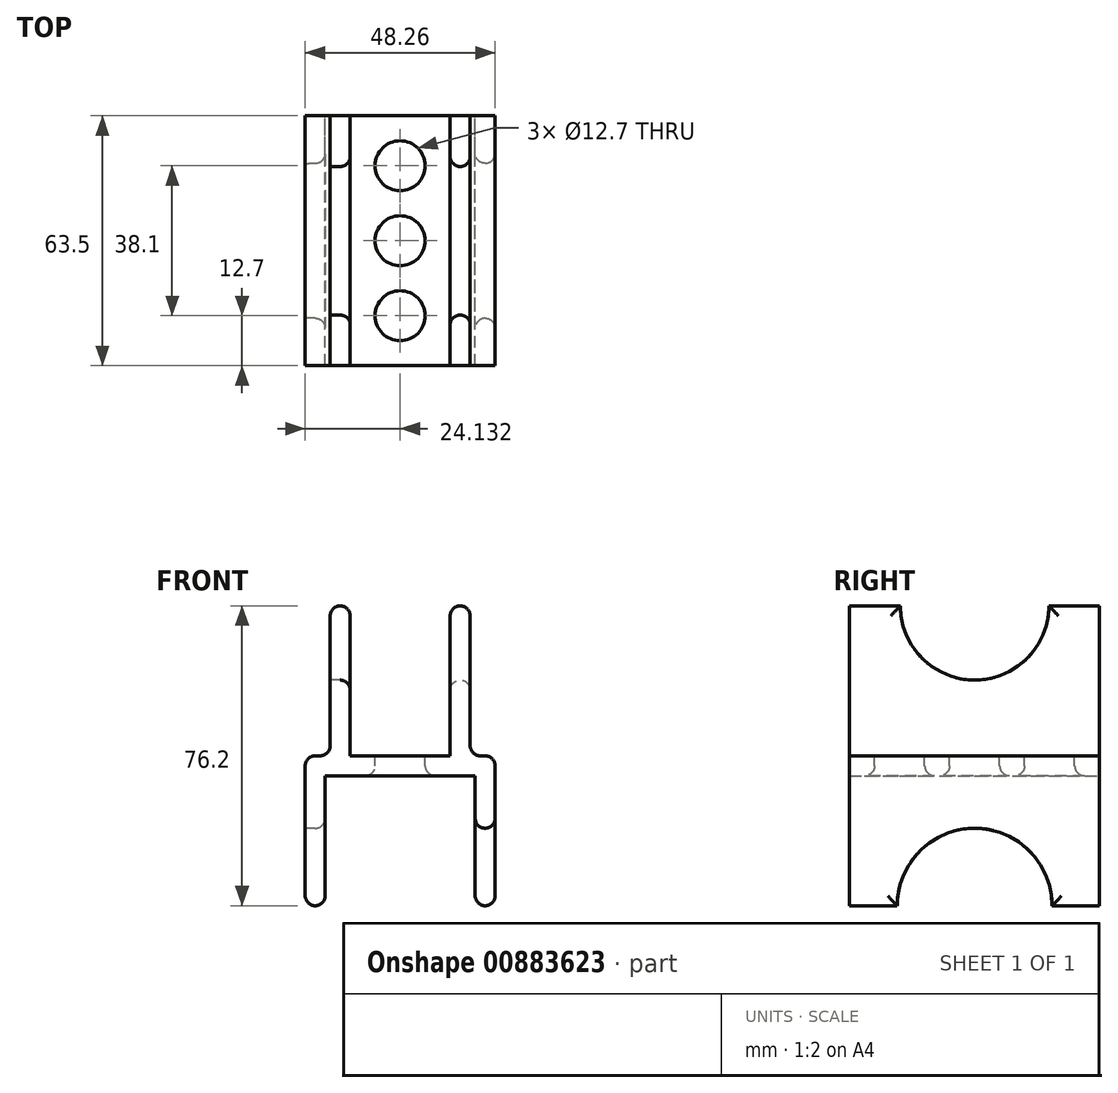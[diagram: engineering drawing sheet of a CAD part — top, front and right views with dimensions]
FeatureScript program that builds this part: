
annotation { "Feature Type Name" : "Feature", "Feature Type Description" : "" }
export const myFeature = defineFeature(function(context is Context, id is Id, definition is map)
    precondition{}
    {
        {
            var Q0;
            Q0=qCreatedBy(makeId("Front.planeOp"),FACE);
            var sketch = newSketch(context, id + "F0", { "sketchPlane" : qUnion([Q0])});
            skLineSegment(sketch, "E0", {"start": v(-15.34, 51.9) * mm, "end": v(-10.26, 51.9) * mm});
            skLineSegment(sketch, "E1", {"start": v(-10.26, 51.9) * mm, "end": v(-10.26, 13.8) * mm});
            skLineSegment(sketch, "E2", {"start": v(-10.26, 13.8) * mm, "end": v(15.14, 13.8) * mm});
            skLineSegment(sketch, "E3", {"start": v(15.14, 13.8) * mm, "end": v(15.14, 51.9) * mm});
            skLineSegment(sketch, "E4", {"start": v(15.14, 51.9) * mm, "end": v(20.22, 51.9) * mm});
            skLineSegment(sketch, "E5", {"start": v(20.22, 51.9) * mm, "end": v(20.22, 13.8) * mm});
            skLineSegment(sketch, "E6", {"start": v(20.22, 13.8) * mm, "end": v(26.57, 13.8) * mm});
            skLineSegment(sketch, "E7", {"start": v(26.57, 13.8) * mm, "end": v(26.57, -24.3) * mm});
            skLineSegment(sketch, "E8", {"start": v(26.57, -24.3) * mm, "end": v(21.5, -24.3) * mm});
            skLineSegment(sketch, "E9", {"start": v(21.5, -24.3) * mm, "end": v(21.5, 8.72) * mm});
            skLineSegment(sketch, "E10", {"start": v(21.5, 8.72) * mm, "end": v(-16.6, 8.72) * mm});
            skLineSegment(sketch, "E11", {"start": v(-16.6, 8.72) * mm, "end": v(-16.6, -24.3) * mm});
            skLineSegment(sketch, "E12", {"start": v(-16.6, -24.3) * mm, "end": v(-21.69, -24.3) * mm});
            skLineSegment(sketch, "E13", {"start": v(-21.69, -24.3) * mm, "end": v(-21.69, 13.8) * mm});
            skLineSegment(sketch, "E14", {"start": v(-21.69, 13.8) * mm, "end": v(-15.34, 13.8) * mm});
            skLineSegment(sketch, "E15", {"start": v(-15.34, 13.8) * mm, "end": v(-15.34, 51.9) * mm});
            skSolve(sketch);
        }
        {
            var Q0;
            Q0=makeQuery(id+"F0.imprint","IMPRINT",FACE,{"disambiguationData":[TD([[makeQuery(id+"F0.imprint","IMPRINT",EDGE,{"derivedFrom":sQuery(id+"F0.wireOp",EDGE,"E0")}),-1.0]])]});
            extrude(context, id + "F1", {"entities" : qUnion([Q0]), "depth" : 63.5 * mm, "offsetDistance" : 25.4 * mm});
        }
        {
            var Q0;
            Q0=makeQuery(id+"F1.opExtrude","SWEPT_FACE",FACE,{"disambiguationData":[OSD([sQuery(id+"F0.wireOp",EDGE,"E13")])]});
            var sketch = newSketch(context, id + "F2", { "sketchPlane" : qUnion([Q0])});
            skCircle(sketch, "E16", {"center": v(31.75, -24.3) * mm, "radius": 19.68 * mm});
            skSolve(sketch);
        }
        {
            var Q0;
            {var subQ0=sQuery(id+"F2.wireOp",EDGE,"E16");var subQ1=makeQuery(id+"F1.opExtrude","SWEPT_EDGE",EDGE,{"disambiguationData":[OSD([sQuery(id+"F0.wireOp",EDGE,"E12"),sQuery(id+"F0.wireOp",EDGE,"E13")])]});var subQ2=makeQuery(id+"F2.imprint","INTERSECT",VERTEX,{"disambiguationData":[OD(0.0)],"derivedFrom":[subQ1,subQ0]});Q0=makeQuery(id+"F2.imprint","IMPRINT",FACE,{"disambiguationData":[TD([[makeQuery(id+"F2.imprint","IMPRINT",EDGE,{"disambiguationData":[TD([[subQ2,1.0]])],"derivedFrom":subQ0}),1.0]])]});}
            extrude(context, id + "F3", {"entities" : qUnion([Q0]), "operationType" : NewBodyOperationType.REMOVE, "endBound" : BoundingType.THROUGH_ALL, "oppositeDirection" : true, "depth" : 25.4 * mm, "offsetDistance" : 25.4 * mm});
        }
        {
            var Q0;
            Q0=makeQuery(id+"F1.opExtrude","SWEPT_FACE",FACE,{"disambiguationData":[OSD([sQuery(id+"F0.wireOp",EDGE,"E15")])]});
            var sketch = newSketch(context, id + "F4", { "sketchPlane" : qUnion([Q0])});
            skCircle(sketch, "E17", {"center": v(31.75, 51.9) * mm, "radius": 18.87 * mm});
            skSolve(sketch);
        }
        {
            var Q0;
            {var subQ0=sQuery(id+"F4.wireOp",EDGE,"E17");var subQ1=makeQuery(id+"F1.opExtrude","SWEPT_EDGE",EDGE,{"disambiguationData":[OSD([sQuery(id+"F0.wireOp",EDGE,"E0"),sQuery(id+"F0.wireOp",EDGE,"E15")])]});var subQ2=makeQuery(id+"F4.imprint","INTERSECT",VERTEX,{"disambiguationData":[OD(0.0)],"derivedFrom":[subQ1,subQ0]});Q0=makeQuery(id+"F4.imprint","IMPRINT",FACE,{"disambiguationData":[TD([[makeQuery(id+"F4.imprint","IMPRINT",EDGE,{"disambiguationData":[TD([[subQ2,-1.0]])],"derivedFrom":subQ0}),1.0]])]});}
            extrude(context, id + "F5", {"entities" : qUnion([Q0]), "operationType" : NewBodyOperationType.REMOVE, "endBound" : BoundingType.THROUGH_ALL, "oppositeDirection" : true, "depth" : 25.4 * mm, "offsetDistance" : 25.4 * mm});
        }
        {
            var Q0;
            Q0=makeQuery(id+"F1.opExtrude","SWEPT_FACE",FACE,{"disambiguationData":[OSD([sQuery(id+"F0.wireOp",EDGE,"E2")])]});
            var sketch = newSketch(context, id + "F6", { "sketchPlane" : qUnion([Q0])});
            skCircle(sketch, "E18", {"center": v(2.44, -12.7) * mm, "radius": 6.35 * mm});
            skCircle(sketch, "E19", {"center": v(2.44, -31.75) * mm, "radius": 6.35 * mm});
            skCircle(sketch, "E20", {"center": v(2.44, -50.8) * mm, "radius": 6.35 * mm});
            skSolve(sketch);
        }
        {
            var Q0;
            Q0=makeQuery(id+"F6.imprint","IMPRINT",FACE,{"disambiguationData":[TD([[makeQuery(id+"F6.imprint","IMPRINT",EDGE,{"derivedFrom":sQuery(id+"F6.wireOp",EDGE,"E20")}),1.0]])]});
            var Q1;
            Q1=makeQuery(id+"F6.imprint","IMPRINT",FACE,{"disambiguationData":[TD([[makeQuery(id+"F6.imprint","IMPRINT",EDGE,{"derivedFrom":sQuery(id+"F6.wireOp",EDGE,"E18")}),1.0]])]});
            var Q2;
            Q2=makeQuery(id+"F6.imprint","IMPRINT",FACE,{"disambiguationData":[TD([[makeQuery(id+"F6.imprint","IMPRINT",EDGE,{"derivedFrom":sQuery(id+"F6.wireOp",EDGE,"E19")}),1.0]])]});
            extrude(context, id + "F7", {"entities" : qUnion([Q0, Q1, Q2]), "operationType" : NewBodyOperationType.REMOVE, "oppositeDirection" : true, "depth" : 25.4 * mm, "offsetDistance" : 25.4 * mm});
        }
        {
            var Q0;
            Q0=makeQuery(id+"F1.opExtrude","SWEPT_EDGE",EDGE,{"disambiguationData":[OSD([sQuery(id+"F0.wireOp",EDGE,"E5"),sQuery(id+"F0.wireOp",EDGE,"E6")])]});
            var Q1;
            Q1=makeQuery(id+"F1.opExtrude","SWEPT_EDGE",EDGE,{"disambiguationData":[OSD([sQuery(id+"F0.wireOp",EDGE,"E6"),sQuery(id+"F0.wireOp",EDGE,"E7")])]});
            var Q2;
            Q2=makeQuery(id+"F1.opExtrude","SWEPT_EDGE",EDGE,{"disambiguationData":[OSD([sQuery(id+"F0.wireOp",EDGE,"E13"),sQuery(id+"F0.wireOp",EDGE,"E14")])]});
            var Q3;
            Q3=makeQuery(id+"F1.opExtrude","SWEPT_EDGE",EDGE,{"disambiguationData":[OSD([sQuery(id+"F0.wireOp",EDGE,"E14"),sQuery(id+"F0.wireOp",EDGE,"E15")])]});
            var Q4;
            {var subQ0=sQuery(id+"F0.wireOp",EDGE,"E4");var subQ1=sQuery(id+"F0.wireOp",EDGE,"E3");Q4=makeQuery(id+"F5.boolean.opBoolean","SPLIT",EDGE,{"disambiguationData":[TD([makeQuery(id+"F1.opExtrude","CAP_FACE",FACE,{"disambiguationData":[OSD([sQuery(id+"F0.wireOp",EDGE,"E0"),sQuery(id+"F0.wireOp",EDGE,"E1"),sQuery(id+"F0.wireOp",EDGE,"E2"),subQ1,subQ0,sQuery(id+"F0.wireOp",EDGE,"E5"),sQuery(id+"F0.wireOp",EDGE,"E6"),sQuery(id+"F0.wireOp",EDGE,"E7"),sQuery(id+"F0.wireOp",EDGE,"E8"),sQuery(id+"F0.wireOp",EDGE,"E9"),sQuery(id+"F0.wireOp",EDGE,"E10"),sQuery(id+"F0.wireOp",EDGE,"E11"),sQuery(id+"F0.wireOp",EDGE,"E12"),sQuery(id+"F0.wireOp",EDGE,"E13"),sQuery(id+"F0.wireOp",EDGE,"E14"),sQuery(id+"F0.wireOp",EDGE,"E15")])],"isStart":false})])],"derivedFrom":makeQuery(id+"F1.opExtrude","SWEPT_EDGE",EDGE,{"disambiguationData":[OSD([subQ1,subQ0])]})});}
            var Q5;
            {var subQ0=sQuery(id+"F0.wireOp",EDGE,"E4");var subQ1=sQuery(id+"F0.wireOp",EDGE,"E3");Q5=makeQuery(id+"F5.boolean.opBoolean","SPLIT",EDGE,{"disambiguationData":[TD([makeQuery(id+"F1.opExtrude","CAP_FACE",FACE,{"disambiguationData":[OSD([sQuery(id+"F0.wireOp",EDGE,"E0"),sQuery(id+"F0.wireOp",EDGE,"E1"),sQuery(id+"F0.wireOp",EDGE,"E2"),subQ1,subQ0,sQuery(id+"F0.wireOp",EDGE,"E5"),sQuery(id+"F0.wireOp",EDGE,"E6"),sQuery(id+"F0.wireOp",EDGE,"E7"),sQuery(id+"F0.wireOp",EDGE,"E8"),sQuery(id+"F0.wireOp",EDGE,"E9"),sQuery(id+"F0.wireOp",EDGE,"E10"),sQuery(id+"F0.wireOp",EDGE,"E11"),sQuery(id+"F0.wireOp",EDGE,"E12"),sQuery(id+"F0.wireOp",EDGE,"E13"),sQuery(id+"F0.wireOp",EDGE,"E14"),sQuery(id+"F0.wireOp",EDGE,"E15")])],"isStart":true})])],"derivedFrom":makeQuery(id+"F1.opExtrude","SWEPT_EDGE",EDGE,{"disambiguationData":[OSD([subQ1,subQ0])]})});}
            var Q6;
            {var subQ0=sQuery(id+"F0.wireOp",EDGE,"E0");var subQ1=sQuery(id+"F0.wireOp",EDGE,"E1");Q6=makeQuery(id+"F5.boolean.opBoolean","SPLIT",EDGE,{"disambiguationData":[TD([makeQuery(id+"F1.opExtrude","CAP_FACE",FACE,{"disambiguationData":[OSD([subQ0,subQ1,sQuery(id+"F0.wireOp",EDGE,"E2"),sQuery(id+"F0.wireOp",EDGE,"E3"),sQuery(id+"F0.wireOp",EDGE,"E4"),sQuery(id+"F0.wireOp",EDGE,"E5"),sQuery(id+"F0.wireOp",EDGE,"E6"),sQuery(id+"F0.wireOp",EDGE,"E7"),sQuery(id+"F0.wireOp",EDGE,"E8"),sQuery(id+"F0.wireOp",EDGE,"E9"),sQuery(id+"F0.wireOp",EDGE,"E10"),sQuery(id+"F0.wireOp",EDGE,"E11"),sQuery(id+"F0.wireOp",EDGE,"E12"),sQuery(id+"F0.wireOp",EDGE,"E13"),sQuery(id+"F0.wireOp",EDGE,"E14"),sQuery(id+"F0.wireOp",EDGE,"E15")])],"isStart":true})])],"derivedFrom":makeQuery(id+"F1.opExtrude","SWEPT_EDGE",EDGE,{"disambiguationData":[OSD([subQ0,subQ1])]})});}
            var Q7;
            {var subQ0=sQuery(id+"F0.wireOp",EDGE,"E0");var subQ1=sQuery(id+"F0.wireOp",EDGE,"E1");Q7=makeQuery(id+"F5.boolean.opBoolean","SPLIT",EDGE,{"disambiguationData":[TD([makeQuery(id+"F1.opExtrude","CAP_FACE",FACE,{"disambiguationData":[OSD([subQ0,subQ1,sQuery(id+"F0.wireOp",EDGE,"E2"),sQuery(id+"F0.wireOp",EDGE,"E3"),sQuery(id+"F0.wireOp",EDGE,"E4"),sQuery(id+"F0.wireOp",EDGE,"E5"),sQuery(id+"F0.wireOp",EDGE,"E6"),sQuery(id+"F0.wireOp",EDGE,"E7"),sQuery(id+"F0.wireOp",EDGE,"E8"),sQuery(id+"F0.wireOp",EDGE,"E9"),sQuery(id+"F0.wireOp",EDGE,"E10"),sQuery(id+"F0.wireOp",EDGE,"E11"),sQuery(id+"F0.wireOp",EDGE,"E12"),sQuery(id+"F0.wireOp",EDGE,"E13"),sQuery(id+"F0.wireOp",EDGE,"E14"),sQuery(id+"F0.wireOp",EDGE,"E15")])],"isStart":false})])],"derivedFrom":makeQuery(id+"F1.opExtrude","SWEPT_EDGE",EDGE,{"disambiguationData":[OSD([subQ0,subQ1])]})});}
            var Q8;
            {var subQ0=sQuery(id+"F0.wireOp",EDGE,"E0");var subQ1=sQuery(id+"F0.wireOp",EDGE,"E15");Q8=makeQuery(id+"F5.boolean.opBoolean","SPLIT",EDGE,{"disambiguationData":[TD([makeQuery(id+"F1.opExtrude","CAP_FACE",FACE,{"disambiguationData":[OSD([subQ0,sQuery(id+"F0.wireOp",EDGE,"E1"),sQuery(id+"F0.wireOp",EDGE,"E2"),sQuery(id+"F0.wireOp",EDGE,"E3"),sQuery(id+"F0.wireOp",EDGE,"E4"),sQuery(id+"F0.wireOp",EDGE,"E5"),sQuery(id+"F0.wireOp",EDGE,"E6"),sQuery(id+"F0.wireOp",EDGE,"E7"),sQuery(id+"F0.wireOp",EDGE,"E8"),sQuery(id+"F0.wireOp",EDGE,"E9"),sQuery(id+"F0.wireOp",EDGE,"E10"),sQuery(id+"F0.wireOp",EDGE,"E11"),sQuery(id+"F0.wireOp",EDGE,"E12"),sQuery(id+"F0.wireOp",EDGE,"E13"),sQuery(id+"F0.wireOp",EDGE,"E14"),subQ1])],"isStart":true})])],"derivedFrom":makeQuery(id+"F1.opExtrude","SWEPT_EDGE",EDGE,{"disambiguationData":[OSD([subQ0,subQ1])]})});}
            var Q9;
            {var subQ0=sQuery(id+"F0.wireOp",EDGE,"E0");var subQ1=sQuery(id+"F0.wireOp",EDGE,"E15");Q9=makeQuery(id+"F5.boolean.opBoolean","SPLIT",EDGE,{"disambiguationData":[TD([makeQuery(id+"F1.opExtrude","CAP_FACE",FACE,{"disambiguationData":[OSD([subQ0,sQuery(id+"F0.wireOp",EDGE,"E1"),sQuery(id+"F0.wireOp",EDGE,"E2"),sQuery(id+"F0.wireOp",EDGE,"E3"),sQuery(id+"F0.wireOp",EDGE,"E4"),sQuery(id+"F0.wireOp",EDGE,"E5"),sQuery(id+"F0.wireOp",EDGE,"E6"),sQuery(id+"F0.wireOp",EDGE,"E7"),sQuery(id+"F0.wireOp",EDGE,"E8"),sQuery(id+"F0.wireOp",EDGE,"E9"),sQuery(id+"F0.wireOp",EDGE,"E10"),sQuery(id+"F0.wireOp",EDGE,"E11"),sQuery(id+"F0.wireOp",EDGE,"E12"),sQuery(id+"F0.wireOp",EDGE,"E13"),sQuery(id+"F0.wireOp",EDGE,"E14"),subQ1])],"isStart":false})])],"derivedFrom":makeQuery(id+"F1.opExtrude","SWEPT_EDGE",EDGE,{"disambiguationData":[OSD([subQ0,subQ1])]})});}
            var Q10;
            {var subQ0=sQuery(id+"F0.wireOp",EDGE,"E5");var subQ1=sQuery(id+"F0.wireOp",EDGE,"E4");Q10=makeQuery(id+"F5.boolean.opBoolean","SPLIT",EDGE,{"disambiguationData":[TD([makeQuery(id+"F1.opExtrude","CAP_FACE",FACE,{"disambiguationData":[OSD([sQuery(id+"F0.wireOp",EDGE,"E0"),sQuery(id+"F0.wireOp",EDGE,"E1"),sQuery(id+"F0.wireOp",EDGE,"E2"),sQuery(id+"F0.wireOp",EDGE,"E3"),subQ1,subQ0,sQuery(id+"F0.wireOp",EDGE,"E6"),sQuery(id+"F0.wireOp",EDGE,"E7"),sQuery(id+"F0.wireOp",EDGE,"E8"),sQuery(id+"F0.wireOp",EDGE,"E9"),sQuery(id+"F0.wireOp",EDGE,"E10"),sQuery(id+"F0.wireOp",EDGE,"E11"),sQuery(id+"F0.wireOp",EDGE,"E12"),sQuery(id+"F0.wireOp",EDGE,"E13"),sQuery(id+"F0.wireOp",EDGE,"E14"),sQuery(id+"F0.wireOp",EDGE,"E15")])],"isStart":false})])],"derivedFrom":makeQuery(id+"F1.opExtrude","SWEPT_EDGE",EDGE,{"disambiguationData":[OSD([subQ1,subQ0])]})});}
            var Q11;
            {var subQ0=sQuery(id+"F0.wireOp",EDGE,"E5");var subQ1=sQuery(id+"F0.wireOp",EDGE,"E4");Q11=makeQuery(id+"F5.boolean.opBoolean","SPLIT",EDGE,{"disambiguationData":[TD([makeQuery(id+"F1.opExtrude","CAP_FACE",FACE,{"disambiguationData":[OSD([sQuery(id+"F0.wireOp",EDGE,"E0"),sQuery(id+"F0.wireOp",EDGE,"E1"),sQuery(id+"F0.wireOp",EDGE,"E2"),sQuery(id+"F0.wireOp",EDGE,"E3"),subQ1,subQ0,sQuery(id+"F0.wireOp",EDGE,"E6"),sQuery(id+"F0.wireOp",EDGE,"E7"),sQuery(id+"F0.wireOp",EDGE,"E8"),sQuery(id+"F0.wireOp",EDGE,"E9"),sQuery(id+"F0.wireOp",EDGE,"E10"),sQuery(id+"F0.wireOp",EDGE,"E11"),sQuery(id+"F0.wireOp",EDGE,"E12"),sQuery(id+"F0.wireOp",EDGE,"E13"),sQuery(id+"F0.wireOp",EDGE,"E14"),sQuery(id+"F0.wireOp",EDGE,"E15")])],"isStart":true})])],"derivedFrom":makeQuery(id+"F1.opExtrude","SWEPT_EDGE",EDGE,{"disambiguationData":[OSD([subQ1,subQ0])]})});}
            var Q12;
            {var subQ0=sQuery(id+"F0.wireOp",EDGE,"E8");var subQ1=sQuery(id+"F0.wireOp",EDGE,"E7");Q12=makeQuery(id+"F3.boolean.opBoolean","SPLIT",EDGE,{"disambiguationData":[TD([makeQuery(id+"F1.opExtrude","CAP_FACE",FACE,{"disambiguationData":[OSD([sQuery(id+"F0.wireOp",EDGE,"E0"),sQuery(id+"F0.wireOp",EDGE,"E1"),sQuery(id+"F0.wireOp",EDGE,"E2"),sQuery(id+"F0.wireOp",EDGE,"E3"),sQuery(id+"F0.wireOp",EDGE,"E4"),sQuery(id+"F0.wireOp",EDGE,"E5"),sQuery(id+"F0.wireOp",EDGE,"E6"),subQ1,subQ0,sQuery(id+"F0.wireOp",EDGE,"E9"),sQuery(id+"F0.wireOp",EDGE,"E10"),sQuery(id+"F0.wireOp",EDGE,"E11"),sQuery(id+"F0.wireOp",EDGE,"E12"),sQuery(id+"F0.wireOp",EDGE,"E13"),sQuery(id+"F0.wireOp",EDGE,"E14"),sQuery(id+"F0.wireOp",EDGE,"E15")])],"isStart":false})])],"derivedFrom":makeQuery(id+"F1.opExtrude","SWEPT_EDGE",EDGE,{"disambiguationData":[OSD([subQ1,subQ0])]})});}
            var Q13;
            {var subQ0=sQuery(id+"F0.wireOp",EDGE,"E9");var subQ1=sQuery(id+"F0.wireOp",EDGE,"E8");Q13=makeQuery(id+"F3.boolean.opBoolean","SPLIT",EDGE,{"disambiguationData":[TD([makeQuery(id+"F1.opExtrude","CAP_FACE",FACE,{"disambiguationData":[OSD([sQuery(id+"F0.wireOp",EDGE,"E0"),sQuery(id+"F0.wireOp",EDGE,"E1"),sQuery(id+"F0.wireOp",EDGE,"E2"),sQuery(id+"F0.wireOp",EDGE,"E3"),sQuery(id+"F0.wireOp",EDGE,"E4"),sQuery(id+"F0.wireOp",EDGE,"E5"),sQuery(id+"F0.wireOp",EDGE,"E6"),sQuery(id+"F0.wireOp",EDGE,"E7"),subQ1,subQ0,sQuery(id+"F0.wireOp",EDGE,"E10"),sQuery(id+"F0.wireOp",EDGE,"E11"),sQuery(id+"F0.wireOp",EDGE,"E12"),sQuery(id+"F0.wireOp",EDGE,"E13"),sQuery(id+"F0.wireOp",EDGE,"E14"),sQuery(id+"F0.wireOp",EDGE,"E15")])],"isStart":false})])],"derivedFrom":makeQuery(id+"F1.opExtrude","SWEPT_EDGE",EDGE,{"disambiguationData":[OSD([subQ1,subQ0])]})});}
            var Q14;
            {var subQ0=sQuery(id+"F0.wireOp",EDGE,"E9");var subQ1=sQuery(id+"F0.wireOp",EDGE,"E8");Q14=makeQuery(id+"F3.boolean.opBoolean","SPLIT",EDGE,{"disambiguationData":[TD([makeQuery(id+"F1.opExtrude","CAP_FACE",FACE,{"disambiguationData":[OSD([sQuery(id+"F0.wireOp",EDGE,"E0"),sQuery(id+"F0.wireOp",EDGE,"E1"),sQuery(id+"F0.wireOp",EDGE,"E2"),sQuery(id+"F0.wireOp",EDGE,"E3"),sQuery(id+"F0.wireOp",EDGE,"E4"),sQuery(id+"F0.wireOp",EDGE,"E5"),sQuery(id+"F0.wireOp",EDGE,"E6"),sQuery(id+"F0.wireOp",EDGE,"E7"),subQ1,subQ0,sQuery(id+"F0.wireOp",EDGE,"E10"),sQuery(id+"F0.wireOp",EDGE,"E11"),sQuery(id+"F0.wireOp",EDGE,"E12"),sQuery(id+"F0.wireOp",EDGE,"E13"),sQuery(id+"F0.wireOp",EDGE,"E14"),sQuery(id+"F0.wireOp",EDGE,"E15")])],"isStart":true})])],"derivedFrom":makeQuery(id+"F1.opExtrude","SWEPT_EDGE",EDGE,{"disambiguationData":[OSD([subQ1,subQ0])]})});}
            var Q15;
            {var subQ0=sQuery(id+"F0.wireOp",EDGE,"E8");var subQ1=sQuery(id+"F0.wireOp",EDGE,"E7");Q15=makeQuery(id+"F3.boolean.opBoolean","SPLIT",EDGE,{"disambiguationData":[TD([makeQuery(id+"F1.opExtrude","CAP_FACE",FACE,{"disambiguationData":[OSD([sQuery(id+"F0.wireOp",EDGE,"E0"),sQuery(id+"F0.wireOp",EDGE,"E1"),sQuery(id+"F0.wireOp",EDGE,"E2"),sQuery(id+"F0.wireOp",EDGE,"E3"),sQuery(id+"F0.wireOp",EDGE,"E4"),sQuery(id+"F0.wireOp",EDGE,"E5"),sQuery(id+"F0.wireOp",EDGE,"E6"),subQ1,subQ0,sQuery(id+"F0.wireOp",EDGE,"E9"),sQuery(id+"F0.wireOp",EDGE,"E10"),sQuery(id+"F0.wireOp",EDGE,"E11"),sQuery(id+"F0.wireOp",EDGE,"E12"),sQuery(id+"F0.wireOp",EDGE,"E13"),sQuery(id+"F0.wireOp",EDGE,"E14"),sQuery(id+"F0.wireOp",EDGE,"E15")])],"isStart":true})])],"derivedFrom":makeQuery(id+"F1.opExtrude","SWEPT_EDGE",EDGE,{"disambiguationData":[OSD([subQ1,subQ0])]})});}
            var Q16;
            {var subQ0=sQuery(id+"F0.wireOp",EDGE,"E12");var subQ1=sQuery(id+"F0.wireOp",EDGE,"E11");Q16=makeQuery(id+"F3.boolean.opBoolean","SPLIT",EDGE,{"disambiguationData":[TD([makeQuery(id+"F1.opExtrude","CAP_FACE",FACE,{"disambiguationData":[OSD([sQuery(id+"F0.wireOp",EDGE,"E0"),sQuery(id+"F0.wireOp",EDGE,"E1"),sQuery(id+"F0.wireOp",EDGE,"E2"),sQuery(id+"F0.wireOp",EDGE,"E3"),sQuery(id+"F0.wireOp",EDGE,"E4"),sQuery(id+"F0.wireOp",EDGE,"E5"),sQuery(id+"F0.wireOp",EDGE,"E6"),sQuery(id+"F0.wireOp",EDGE,"E7"),sQuery(id+"F0.wireOp",EDGE,"E8"),sQuery(id+"F0.wireOp",EDGE,"E9"),sQuery(id+"F0.wireOp",EDGE,"E10"),subQ1,subQ0,sQuery(id+"F0.wireOp",EDGE,"E13"),sQuery(id+"F0.wireOp",EDGE,"E14"),sQuery(id+"F0.wireOp",EDGE,"E15")])],"isStart":true})])],"derivedFrom":makeQuery(id+"F1.opExtrude","SWEPT_EDGE",EDGE,{"disambiguationData":[OSD([subQ1,subQ0])]})});}
            var Q17;
            {var subQ0=sQuery(id+"F0.wireOp",EDGE,"E13");var subQ1=sQuery(id+"F0.wireOp",EDGE,"E12");Q17=makeQuery(id+"F3.boolean.opBoolean","SPLIT",EDGE,{"disambiguationData":[TD([makeQuery(id+"F1.opExtrude","CAP_FACE",FACE,{"disambiguationData":[OSD([sQuery(id+"F0.wireOp",EDGE,"E0"),sQuery(id+"F0.wireOp",EDGE,"E1"),sQuery(id+"F0.wireOp",EDGE,"E2"),sQuery(id+"F0.wireOp",EDGE,"E3"),sQuery(id+"F0.wireOp",EDGE,"E4"),sQuery(id+"F0.wireOp",EDGE,"E5"),sQuery(id+"F0.wireOp",EDGE,"E6"),sQuery(id+"F0.wireOp",EDGE,"E7"),sQuery(id+"F0.wireOp",EDGE,"E8"),sQuery(id+"F0.wireOp",EDGE,"E9"),sQuery(id+"F0.wireOp",EDGE,"E10"),sQuery(id+"F0.wireOp",EDGE,"E11"),subQ1,subQ0,sQuery(id+"F0.wireOp",EDGE,"E14"),sQuery(id+"F0.wireOp",EDGE,"E15")])],"isStart":true})])],"derivedFrom":makeQuery(id+"F1.opExtrude","SWEPT_EDGE",EDGE,{"disambiguationData":[OSD([subQ1,subQ0])]})});}
            var Q18;
            {var subQ0=sQuery(id+"F0.wireOp",EDGE,"E13");var subQ1=sQuery(id+"F0.wireOp",EDGE,"E12");Q18=makeQuery(id+"F3.boolean.opBoolean","SPLIT",EDGE,{"disambiguationData":[TD([makeQuery(id+"F1.opExtrude","CAP_FACE",FACE,{"disambiguationData":[OSD([sQuery(id+"F0.wireOp",EDGE,"E0"),sQuery(id+"F0.wireOp",EDGE,"E1"),sQuery(id+"F0.wireOp",EDGE,"E2"),sQuery(id+"F0.wireOp",EDGE,"E3"),sQuery(id+"F0.wireOp",EDGE,"E4"),sQuery(id+"F0.wireOp",EDGE,"E5"),sQuery(id+"F0.wireOp",EDGE,"E6"),sQuery(id+"F0.wireOp",EDGE,"E7"),sQuery(id+"F0.wireOp",EDGE,"E8"),sQuery(id+"F0.wireOp",EDGE,"E9"),sQuery(id+"F0.wireOp",EDGE,"E10"),sQuery(id+"F0.wireOp",EDGE,"E11"),subQ1,subQ0,sQuery(id+"F0.wireOp",EDGE,"E14"),sQuery(id+"F0.wireOp",EDGE,"E15")])],"isStart":false})])],"derivedFrom":makeQuery(id+"F1.opExtrude","SWEPT_EDGE",EDGE,{"disambiguationData":[OSD([subQ1,subQ0])]})});}
            var Q19;
            {var subQ0=sQuery(id+"F0.wireOp",EDGE,"E12");var subQ1=sQuery(id+"F0.wireOp",EDGE,"E11");Q19=makeQuery(id+"F3.boolean.opBoolean","SPLIT",EDGE,{"disambiguationData":[TD([makeQuery(id+"F1.opExtrude","CAP_FACE",FACE,{"disambiguationData":[OSD([sQuery(id+"F0.wireOp",EDGE,"E0"),sQuery(id+"F0.wireOp",EDGE,"E1"),sQuery(id+"F0.wireOp",EDGE,"E2"),sQuery(id+"F0.wireOp",EDGE,"E3"),sQuery(id+"F0.wireOp",EDGE,"E4"),sQuery(id+"F0.wireOp",EDGE,"E5"),sQuery(id+"F0.wireOp",EDGE,"E6"),sQuery(id+"F0.wireOp",EDGE,"E7"),sQuery(id+"F0.wireOp",EDGE,"E8"),sQuery(id+"F0.wireOp",EDGE,"E9"),sQuery(id+"F0.wireOp",EDGE,"E10"),subQ1,subQ0,sQuery(id+"F0.wireOp",EDGE,"E13"),sQuery(id+"F0.wireOp",EDGE,"E14"),sQuery(id+"F0.wireOp",EDGE,"E15")])],"isStart":false})])],"derivedFrom":makeQuery(id+"F1.opExtrude","SWEPT_EDGE",EDGE,{"disambiguationData":[OSD([subQ1,subQ0])]})});}
            var Q20;
            Q20=makeQuery(id+"F5.boolean.opBoolean","INTERSECT",EDGE,{"derivedFrom":[makeQuery(id+"F1.opExtrude","SWEPT_FACE",FACE,{"disambiguationData":[OSD([sQuery(id+"F0.wireOp",EDGE,"E1")])]}),makeQuery(id+"F5.opExtrude","SWEPT_FACE",FACE,{"disambiguationData":[OSD([sQuery(id+"F4.wireOp",EDGE,"E17")])]})]});
            var Q21;
            Q21=makeQuery(id+"F5.boolean.opBoolean","COPY",EDGE,{"derivedFrom":makeQuery(id+"F5.opExtrude","CAP_EDGE",EDGE,{"disambiguationData":[OSD([sQuery(id+"F4.wireOp",EDGE,"E17")])],"isStart":true})});
            var Q22;
            Q22=makeQuery(id+"F5.boolean.opBoolean","INTERSECT",EDGE,{"derivedFrom":[makeQuery(id+"F1.opExtrude","SWEPT_FACE",FACE,{"disambiguationData":[OSD([sQuery(id+"F0.wireOp",EDGE,"E5")])]}),makeQuery(id+"F5.opExtrude","SWEPT_FACE",FACE,{"disambiguationData":[OSD([sQuery(id+"F4.wireOp",EDGE,"E17")])]})]});
            var Q23;
            Q23=makeQuery(id+"F5.boolean.opBoolean","INTERSECT",EDGE,{"derivedFrom":[makeQuery(id+"F1.opExtrude","SWEPT_FACE",FACE,{"disambiguationData":[OSD([sQuery(id+"F0.wireOp",EDGE,"E3")])]}),makeQuery(id+"F5.opExtrude","SWEPT_FACE",FACE,{"disambiguationData":[OSD([sQuery(id+"F4.wireOp",EDGE,"E17")])]})]});
            var Q24;
            Q24=makeQuery(id+"F3.boolean.opBoolean","INTERSECT",EDGE,{"derivedFrom":[makeQuery(id+"F1.opExtrude","SWEPT_FACE",FACE,{"disambiguationData":[OSD([sQuery(id+"F0.wireOp",EDGE,"E7")])]}),makeQuery(id+"F3.opExtrude","SWEPT_FACE",FACE,{"disambiguationData":[OSD([sQuery(id+"F2.wireOp",EDGE,"E16")])]})]});
            var Q25;
            Q25=makeQuery(id+"F3.boolean.opBoolean","INTERSECT",EDGE,{"derivedFrom":[makeQuery(id+"F1.opExtrude","SWEPT_FACE",FACE,{"disambiguationData":[OSD([sQuery(id+"F0.wireOp",EDGE,"E9")])]}),makeQuery(id+"F3.opExtrude","SWEPT_FACE",FACE,{"disambiguationData":[OSD([sQuery(id+"F2.wireOp",EDGE,"E16")])]})]});
            var Q26;
            Q26=makeQuery(id+"F3.boolean.opBoolean","INTERSECT",EDGE,{"derivedFrom":[makeQuery(id+"F1.opExtrude","SWEPT_FACE",FACE,{"disambiguationData":[OSD([sQuery(id+"F0.wireOp",EDGE,"E11")])]}),makeQuery(id+"F3.opExtrude","SWEPT_FACE",FACE,{"disambiguationData":[OSD([sQuery(id+"F2.wireOp",EDGE,"E16")])]})]});
            var Q27;
            Q27=makeQuery(id+"F3.boolean.opBoolean","COPY",EDGE,{"derivedFrom":makeQuery(id+"F3.opExtrude","CAP_EDGE",EDGE,{"disambiguationData":[OSD([sQuery(id+"F2.wireOp",EDGE,"E16")])],"isStart":true})});
            var Q28;
            Q28=makeQuery(id+"F7.boolean.opBoolean","COPY",EDGE,{"derivedFrom":makeQuery(id+"F7.opExtrude","CAP_EDGE",EDGE,{"disambiguationData":[OSD([sQuery(id+"F6.wireOp",EDGE,"E20")])],"isStart":true})});
            var Q29;
            Q29=makeQuery(id+"F7.boolean.opBoolean","COPY",EDGE,{"derivedFrom":makeQuery(id+"F7.opExtrude","CAP_EDGE",EDGE,{"disambiguationData":[OSD([sQuery(id+"F6.wireOp",EDGE,"E19")])],"isStart":true})});
            var Q30;
            Q30=makeQuery(id+"F7.boolean.opBoolean","COPY",EDGE,{"derivedFrom":makeQuery(id+"F7.opExtrude","CAP_EDGE",EDGE,{"disambiguationData":[OSD([sQuery(id+"F6.wireOp",EDGE,"E18")])],"isStart":true})});
            var Q31;
            Q31=makeQuery(id+"F7.boolean.opBoolean","INTERSECT",EDGE,{"derivedFrom":[makeQuery(id+"F1.opExtrude","SWEPT_FACE",FACE,{"disambiguationData":[OSD([sQuery(id+"F0.wireOp",EDGE,"E10")])]}),makeQuery(id+"F7.opExtrude","SWEPT_FACE",FACE,{"disambiguationData":[OSD([sQuery(id+"F6.wireOp",EDGE,"E20")])]})]});
            var Q32;
            Q32=makeQuery(id+"F7.boolean.opBoolean","INTERSECT",EDGE,{"derivedFrom":[makeQuery(id+"F1.opExtrude","SWEPT_FACE",FACE,{"disambiguationData":[OSD([sQuery(id+"F0.wireOp",EDGE,"E10")])]}),makeQuery(id+"F7.opExtrude","SWEPT_FACE",FACE,{"disambiguationData":[OSD([sQuery(id+"F6.wireOp",EDGE,"E19")])]})]});
            var Q33;
            Q33=makeQuery(id+"F7.boolean.opBoolean","INTERSECT",EDGE,{"derivedFrom":[makeQuery(id+"F1.opExtrude","SWEPT_FACE",FACE,{"disambiguationData":[OSD([sQuery(id+"F0.wireOp",EDGE,"E10")])]}),makeQuery(id+"F7.opExtrude","SWEPT_FACE",FACE,{"disambiguationData":[OSD([sQuery(id+"F6.wireOp",EDGE,"E18")])]})]});
            fillet(context, id + "F8", {"entities" : qUnion([Q0, Q1, Q2, Q3, Q4, Q5, Q6, Q7, Q8, Q9, Q10, Q11, Q12, Q13, Q14, Q15, Q16, Q17, Q18, Q19, Q20, Q21, Q22, Q23, Q24, Q25, Q26, Q27, Q28, Q29, Q30, Q31, Q32, Q33]), "radius" : 2.54 * mm, "tangentPropagation" : true, "allowEdgeOverflow" : false});
        }
    });
